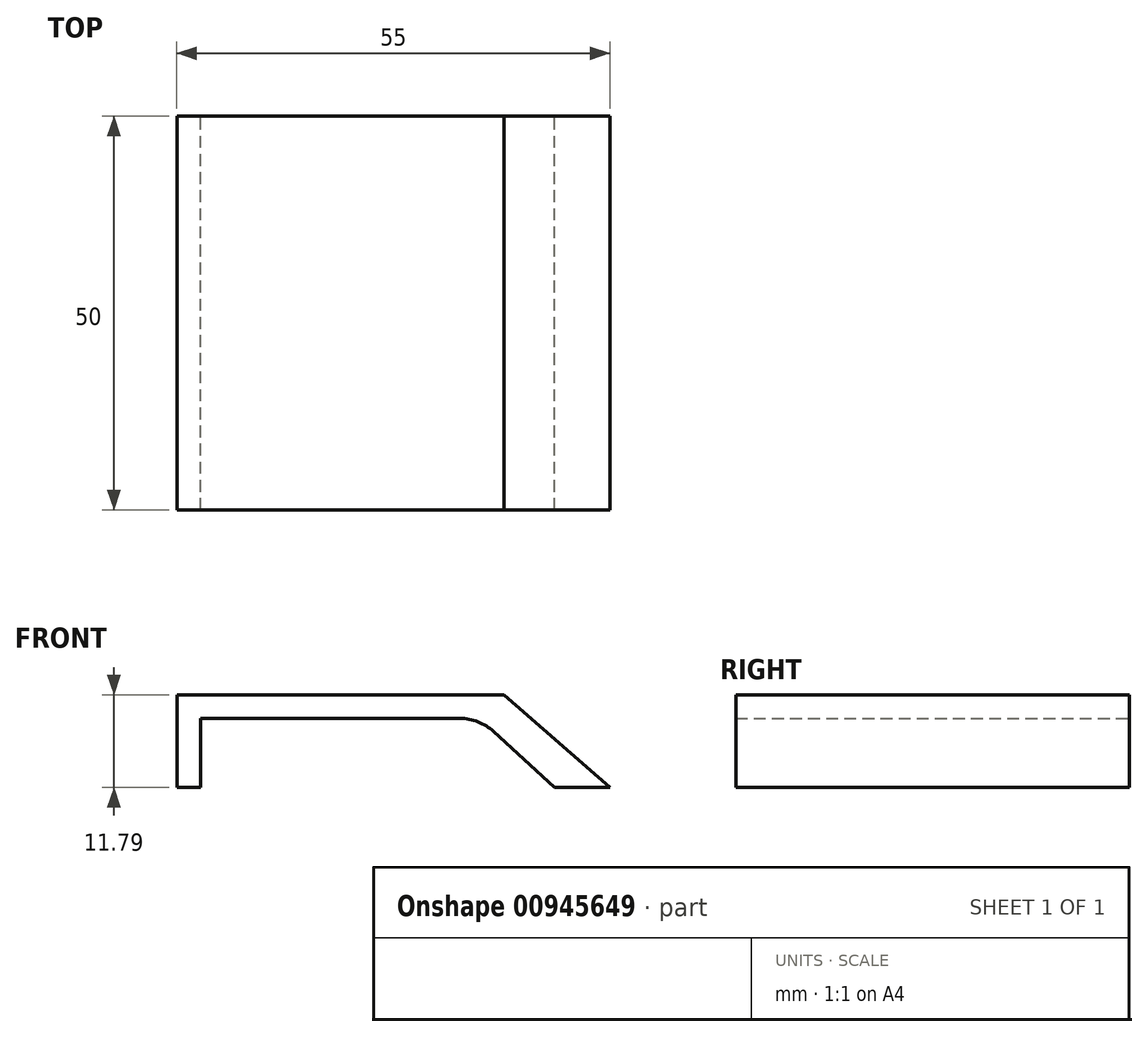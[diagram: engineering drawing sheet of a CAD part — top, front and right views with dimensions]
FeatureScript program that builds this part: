
annotation { "Feature Type Name" : "Feature", "Feature Type Description" : "" }
export const myFeature = defineFeature(function(context is Context, id is Id, definition is map)
    precondition{}
    {
        {
            var Q0;
            Q0=qCreatedBy(makeId("Front.planeOp"),FACE);
            var sketch = newSketch(context, id + "F0", { "sketchPlane" : qUnion([Q0])});
            skLineSegment(sketch, "E0", {"start": v(-20.33, 0) * mm, "end": v(-20.33, 11.8) * mm});
            skLineSegment(sketch, "E1", {"start": v(-20.33, 11.8) * mm, "end": v(21.22, 11.8) * mm});
            skLineSegment(sketch, "E2", {"start": v(21.22, 11.8) * mm, "end": v(34.67, 0) * mm});
            skLineSegment(sketch, "E3", {"start": v(34.67, 0) * mm, "end": v(27.67, 0) * mm});
            skLineSegment(sketch, "E4", {"start": v(27.67, 0) * mm, "end": v(19.93, 7.12) * mm});
            skLineSegment(sketch, "E5", {"start": v(15.63, 8.8) * mm, "end": v(-17.33, 8.8) * mm});
            skLineSegment(sketch, "E6", {"start": v(-17.33, 8.8) * mm, "end": v(-17.33, 0) * mm});
            skLineSegment(sketch, "E7", {"start": v(-17.33, 0) * mm, "end": v(-20.33, 0) * mm});
            skPoint(sketch, "E8.visualSharp", {"position": v(18.1, 8.8) * mm});
            skArc(sketch, "E8.filletArc", {"start": v(19.93, 7.12) * mm, "mid": v(17.93, 8.36) * mm, "end": v(15.63, 8.8) * mm});
            skSolve(sketch);
        }
        {
            var Q0;
            Q0=makeQuery(id+"F0.imprint","IMPRINT",FACE,{"disambiguationData":[TD([[makeQuery(id+"F0.imprint","IMPRINT",EDGE,{"derivedFrom":sQuery(id+"F0.wireOp",EDGE,"E0")}),-1.0]])]});
            extrude(context, id + "F1", {"entities" : qUnion([Q0]), "depth" : 50 * mm, "offsetDistance" : 25 * mm});
        }
    });
